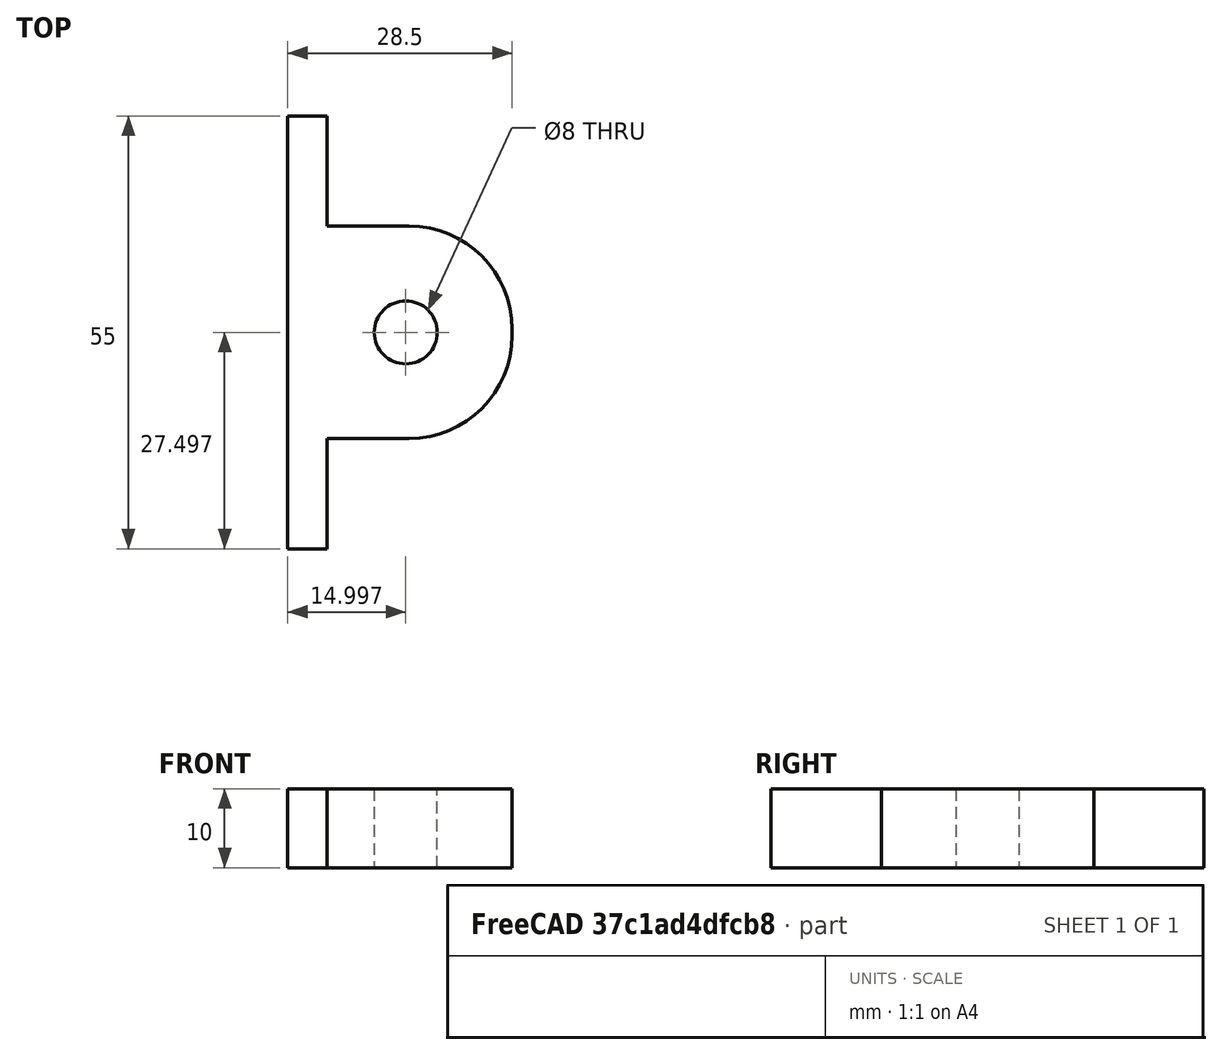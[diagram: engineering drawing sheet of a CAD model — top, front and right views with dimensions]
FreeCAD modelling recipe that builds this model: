
FCSTD DOCUMENT  (FreeCAD 0.17R13522 (Git))
Label: rolamentoKP08
License: All rights reserved
LicenseURL: http://en.wikipedia.org/wiki/All_rights_reserved
objects: Sketcher::SketchObject×1, Part::Extrusion×1
note: 2 computed .brp shape members not serialized (recipe doc carries the construction recipe); baked Part::Feature solids carry a one-line shape summary decoded from their .brp

FEATURE [Sketcher::SketchObject] Sketch
  sketch-geometry (11):
    g0: LineSegment StartX=18.3167 StartY=55.7169 StartZ=0 EndX=18.3167 EndY=0.716924 EndZ=0
    g1: LineSegment StartX=18.3167 StartY=0.716924 StartZ=0 EndX=23.3167 EndY=0.716924 EndZ=0
    g2: LineSegment StartX=23.3167 StartY=0.716924 StartZ=0 EndX=23.3167 EndY=14.7169 EndZ=0
    g3: LineSegment StartX=23.3167 StartY=14.7169 StartZ=0 EndX=33.7413 EndY=14.7169 EndZ=0
    g4: LineSegment StartX=46.8167 StartY=27.7924 StartZ=0 EndX=46.8167 EndY=28.6414 EndZ=0
    g5: LineSegment StartX=33.7413 StartY=41.7169 StartZ=0 EndX=23.3167 EndY=41.7169 EndZ=0
    g6: LineSegment StartX=23.3167 StartY=41.7169 StartZ=0 EndX=23.3167 EndY=55.7169 EndZ=0
    g7: LineSegment StartX=23.3167 StartY=55.7169 StartZ=0 EndX=18.3167 EndY=55.7169 EndZ=0
    g8: Circle CenterX=33.3167 CenterY=28.2169 CenterZ=0 NormalX=0 NormalY=0 NormalZ=1 AngleXU=0 Radius=4
    g9: ArcOfCircle CenterX=33.7413 CenterY=27.7924 CenterZ=0 NormalX=0 NormalY=0 NormalZ=1 AngleXU=0 Radius=13.0755 StartAngle=4.71239 EndAngle=6.28319
    g10: ArcOfCircle CenterX=33.7413 CenterY=28.6414 CenterZ=0 NormalX=0 NormalY=0 NormalZ=1 AngleXU=0 Radius=13.0755 StartAngle=0 EndAngle=1.5708
  constraints (28):
    c: Vertical(g0)
    c: Coincident(g0,g1)
    c: Horizontal(g1)
    c: Coincident(g1,g2)
    c: Vertical(g2)
    c: Coincident(g2,g3)
    c: Horizontal(g3)
    c: Vertical(g4)
    c: Horizontal(g5)
    c: Coincident(g5,g6)
    c: Vertical(g6)
    c: Coincident(g6,g7)
    c: Coincident(g7,g0)
    c: Horizontal(g7)
    c: DistanceY(g0,g0) = 55
    c: DistanceX(g7,g7) = 5
    c: Equal(g7,g1)
    c: Radius(g8) = 4
    c: Distance(g8,g0) = 15
    c: Equal(g6,g2)
    c: Distance(g8,g4) = 13.5
    c: Distance(g8,g5) = 13.5
    c: Distance(g8,g3) = 13.5
    c: Tangent(g4,g9) = -1.5708
    c: Tangent(g3,g9) = -1.5708
    c: Tangent(g5,g10) = -1.5708
    c: Tangent(g4,g10) = -1.5708
    c: Equal(g10,g9)
FEATURE [Part::Extrusion] Extrude  label="KP08"
  Base = -> Sketch
  Dir = (0,0,13)
  DirMode = 0
  FaceMakerClass = Part::FaceMakerBullseye
  LengthFwd = 10
  LengthRev = 0
  Solid = true
  Symmetric = false
